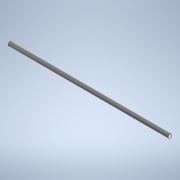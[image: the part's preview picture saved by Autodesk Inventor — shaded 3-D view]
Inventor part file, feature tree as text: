
AUTODESK INVENTOR PART (.ipt)
format: ipt  version: 2021 (Build 250183000, 183)  size: 101,888 bytes
history: native  units: in
note: dims shown in document units (in); Inventor stores cm internally (conversion verified against a paired STEP export)
features: extrude x1, sketch x1
ambient origin geometry x8: Origin, YZ Plane, XZ Plane, XY Plane, X Axis, Y Axis, Z Axis, Center Point
bodies: Solid1 (feature_tree)
feature tree (2):
  extrude  "Extrusion1"  Depth=0.203in TaperAngle=0.0deg
  sketch  "Sketch1"  dims[d0=0.005in d1=0.203in d2=0.0in]
